# Revit family: LUXI_WATERPROOF LIGHT_VT
name_source: partatom
category: Apparecchi per illuminazione
revit_build: Autodesk Revit 2016 (Build: 20161004_0715(x64)
units: mm (PartAtom-declared; Revit-internal decimal feet)

## family parameters
Condiviso = No
Host = Superficie
Numero OmniClass = 23.80.70.00
Punto di calcolo locali = Sì
Quota connettore circolare = Usa diametro
Sorgente d'illuminazione = Sì
Taglio con vuoti quando caricato = No
Tipo di parte = Normale
Titolo OmniClass = Lighting

## types (4) — shared parameters
Angolo inclinazione = -90.00°
CRI = ≥80 (typ.)
Carico apparente = 70 VA
Certifications = CE / RohS
Color = Grey
Descrizione = Waterproof ceiling
Dust and water protection rating = IP 66
Emetti da larghezza rettangolo = 83 mm
Emetti da lunghezza rettangolo = 1430 mm  [stored 4.6916 ft]
Energy class = A+
Filtro dei colori = 16777215
H = 89 mm  [stored 0.291995 ft]
IFCExportAs = IfcLightFixtureType
Impact rating = IK07 (2 Joule)
Installation = Wall / ceiling
Length = 1490 mm  [stored 4.88845 ft]
Lifetime = L70B20 50.000h
Light distribution = Downlight
Light source = LED SMD
Masterformat 2016 code = 26.50.00
Masterformat 2016 description = Lighting
Material 1 = Galvanized Sheet Steel
Material 2 = Galvanized Sheet Steel
Modello = WT Series | Waterproof Light
OFF1 = 30 mm  [stored 0.0984252 ft]
Operating temperature = -25°C / +40°C
Photobiological risk group = RG0
Power factor = ≥0,95 (typ.)
Power supply = Included
Produttore = Luxi Illuminazione S.r.l.
Prospetto di default = 2000 mm  [stored 6.56168 ft]
Protection class = I
Rated supply voltage = 220-240V AC / 50-60 Hz
Rendi la forma visibile nel rendering = No
Review = 3
Size = 1490x112x89
Step MacAdam (SDCM) = <4
URL = https://www.luxi.lighting
Uniclass 2015 code = EF_70_80
Uniclass 2015 description = Lighting
Variazione temperatura colore lampada con luminosità attenuata = <Nessuno>
Warranty = 5 years
Wattage = 70 W
Weight = 4.80 kg
Width = 112 mm  [stored 0.367454 ft]

## per-type parameters (varying)
| type | Dimming | File diagramma fotometrico | Material 3 | Optics |
| WPVT070090G840 |  | WPVT070090G840 Luxi Serie VT 70W BA90X90 1500MM GR 840.IES | Polycarbonate | 90° |
| WPVT070411G840 |  | WPVT070411G840 Luxi Serie VT 70W BA40X110 1500MM GR 840.IES | Glass | 40X110° |
| WPVT070090G840DA | DALI | WPVT070090G840 Luxi Serie VT 70W BA90X90 1500MM GR 840.IES | Polycarbonate | 90° |
| WPVT070411G840DA | DALI | WPVT070411G840 Luxi Serie VT 70W BA40X110 1500MM GR 840.IES | Glass | 40X110° |

note: column(s) folded — value = type name in every type: Code

note: [stored X ft] marks values corroborated as IEEE doubles in the binary element streams (Revit-internal decimal feet)
